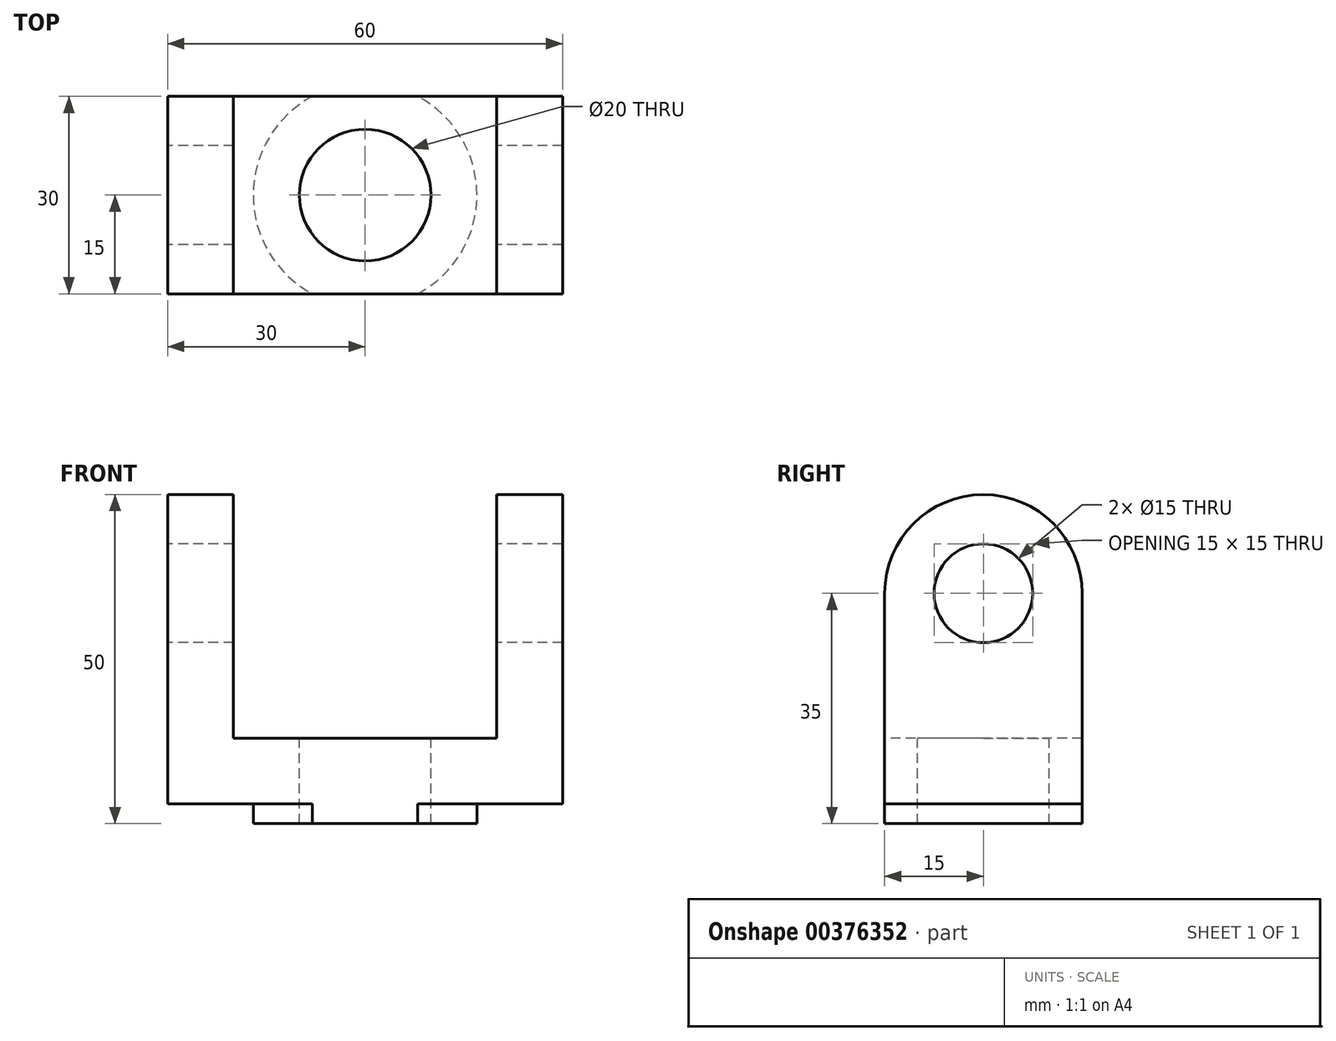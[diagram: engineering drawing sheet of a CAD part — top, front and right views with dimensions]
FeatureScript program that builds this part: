
annotation { "Feature Type Name" : "Feature", "Feature Type Description" : "" }
export const myFeature = defineFeature(function(context is Context, id is Id, definition is map)
    precondition{}
    {
        {
            var Q0;
            Q0=qCreatedBy(makeId("Right.planeOp"),FACE);
            var sketch = newSketch(context, id + "F0", { "sketchPlane" : qUnion([Q0])});
            skCircle(sketch, "E0", {"center": v(0, 0) * mm, "radius": 7.5 * mm});
            skLineSegment(sketch, "E1", {"start": v(-15, -32) * mm, "end": v(15, -32) * mm});
            skLineSegment(sketch, "E2", {"start": v(15, -32) * mm, "end": v(15, 0) * mm});
            skLineSegment(sketch, "E3", {"start": v(-15, -32) * mm, "end": v(-15, 0) * mm});
            skArc(sketch, "E4", {"start": v(-15, 0) * mm, "mid": v(0, 15) * mm, "end": v(15, 0) * mm});
            skSolve(sketch);
        }
        {
            var Q0;
            Q0 = qSketchRegion(id + "F0", true);
            extrude(context, id + "F1", {"entities" : qUnion([Q0]), "endBound" : BoundingType.SYMMETRIC, "depth" : 60 * mm});
        }
        {
            var Q0;
            Q0=qCreatedBy(makeId("Front.planeOp"),FACE);
            var sketch = newSketch(context, id + "F2", { "sketchPlane" : qUnion([Q0])});
            skLineSegment(sketch, "E5.bottom", {"start": v(-20, 26.86) * mm, "end": v(20, 26.86) * mm});
            skLineSegment(sketch, "E5.top", {"start": v(-20, -22) * mm, "end": v(20, -22) * mm});
            skLineSegment(sketch, "E5.left", {"start": v(-20, 26.86) * mm, "end": v(-20, -22) * mm});
            skLineSegment(sketch, "E5.right", {"start": v(20, 26.86) * mm, "end": v(20, -22) * mm});
            skSolve(sketch);
        }
        {
            var Q0;
            Q0 = qSketchRegion(id + "F2", true);
            extrude(context, id + "F3", {"entities" : qUnion([Q0]), "operationType" : NewBodyOperationType.REMOVE, "endBound" : BoundingType.THROUGH_ALL, "oppositeDirection" : true, "depth" : 25 * mm, "hasSecondDirection" : true, "secondDirectionBound" : SecondDirectionBoundingType.THROUGH_ALL, "secondDirectionOppositeDirection" : false, "secondDirectionDepth" : 25 * mm});
        }
        {
            var Q0;
            Q0=qCreatedBy(makeId("Top.planeOp"),FACE);
            var sketch = newSketch(context, id + "F4", { "sketchPlane" : qUnion([Q0])});
            skCircle(sketch, "E6", {"center": v(0, 0) * mm, "radius": 10 * mm});
            skSolve(sketch);
        }
        {
            var Q0;
            Q0 = qSketchRegion(id + "F4", true);
            extrude(context, id + "F5", {"entities" : qUnion([Q0]), "operationType" : NewBodyOperationType.REMOVE, "endBound" : BoundingType.THROUGH_ALL, "oppositeDirection" : true, "depth" : 25 * mm});
        }
        {
            var Q0;
            Q0=makeQuery(id+"F1.opExtrude","SWEPT_FACE",FACE,{"disambiguationData":[OSD([sQuery(id+"F0.wireOp",EDGE,"E1")])]});
            var sketch = newSketch(context, id + "F6", { "sketchPlane" : qUnion([Q0])});
            skCircle(sketch, "E7", {"center": v(0, 0) * mm, "radius": 20 * mm});
            skSolve(sketch);
        }
        {
            var Q0;
            {var subQ0=sQuery(id+"F6.wireOp",EDGE,"E7");var subQ1=makeQuery(id+"F1.opExtrude","SWEPT_EDGE",EDGE,{"disambiguationData":[OSD([sQuery(id+"F0.wireOp",EDGE,"E1"),sQuery(id+"F0.wireOp",EDGE,"E2")])]});var subQ2=makeQuery(id+"F6.imprint","INTERSECT",VERTEX,{"disambiguationData":[OD(0.0)],"derivedFrom":[subQ1,subQ0]});Q0=makeQuery(id+"F6.imprint","IMPRINT",FACE,{"disambiguationData":[TD([[makeQuery(id+"F6.imprint","IMPRINT",EDGE,{"disambiguationData":[TD([[subQ2,-1.0]])],"derivedFrom":subQ0}),1.0]])]});}
            var Q1;
            {var subQ0=sQuery(id+"F6.wireOp",EDGE,"E7");var subQ1=makeQuery(id+"F1.opExtrude","SWEPT_EDGE",EDGE,{"disambiguationData":[OSD([sQuery(id+"F0.wireOp",EDGE,"E1"),sQuery(id+"F0.wireOp",EDGE,"E3")])]});var subQ2=makeQuery(id+"F6.imprint","INTERSECT",VERTEX,{"disambiguationData":[OD(0.0)],"derivedFrom":[subQ1,subQ0]});Q1=makeQuery(id+"F6.imprint","IMPRINT",FACE,{"disambiguationData":[TD([[makeQuery(id+"F6.imprint","IMPRINT",EDGE,{"disambiguationData":[TD([[subQ2,1.0]])],"derivedFrom":subQ0}),1.0]])]});}
            extrude(context, id + "F7", {"entities" : qUnion([Q0, Q1]), "operationType" : NewBodyOperationType.ADD, "oppositeDirection" : true, "depth" : 10 * mm});
        }
        {
            var Q0;
            {var subQ0=sQuery(id+"F6.wireOp",EDGE,"E7");var subQ1=sQuery(id+"F0.wireOp",EDGE,"E1");Q0=makeQuery(id+"F7.boolean.opBoolean","MERGE",FACE,{"derivedFrom":[makeQuery(id+"F1.opExtrude","SWEPT_FACE",FACE,{"disambiguationData":[OSD([subQ1])]}),makeQuery(id+"F7.opExtrude","CAP_FACE",FACE,{"disambiguationData":[OSD([subQ1,sQuery(id+"F0.wireOp",EDGE,"E3"),subQ0])],"isStart":true}),makeQuery(id+"F7.opExtrude","CAP_FACE",FACE,{"disambiguationData":[OSD([subQ1,sQuery(id+"F0.wireOp",EDGE,"E2"),subQ0])],"isStart":true})]});}
            var sketch = newSketch(context, id + "F8", { "sketchPlane" : qUnion([Q0])});
            skCircle(sketch, "E8", {"center": v(0, 0) * mm, "radius": 17 * mm});
            skSolve(sketch);
        }
        {
            var Q0;
            Q0=makeQuery(id+"F8.imprint","IMPRINT",FACE,{"disambiguationData":[TD([[makeQuery(id+"F8.imprint","IMPRINT",EDGE,{"derivedFrom":sQuery(id+"F8.wireOp",EDGE,"E8")}),1.0]])]});
            extrude(context, id + "F9", {"entities" : qUnion([Q0]), "operationType" : NewBodyOperationType.ADD, "depth" : 3 * mm});
        }
    });
